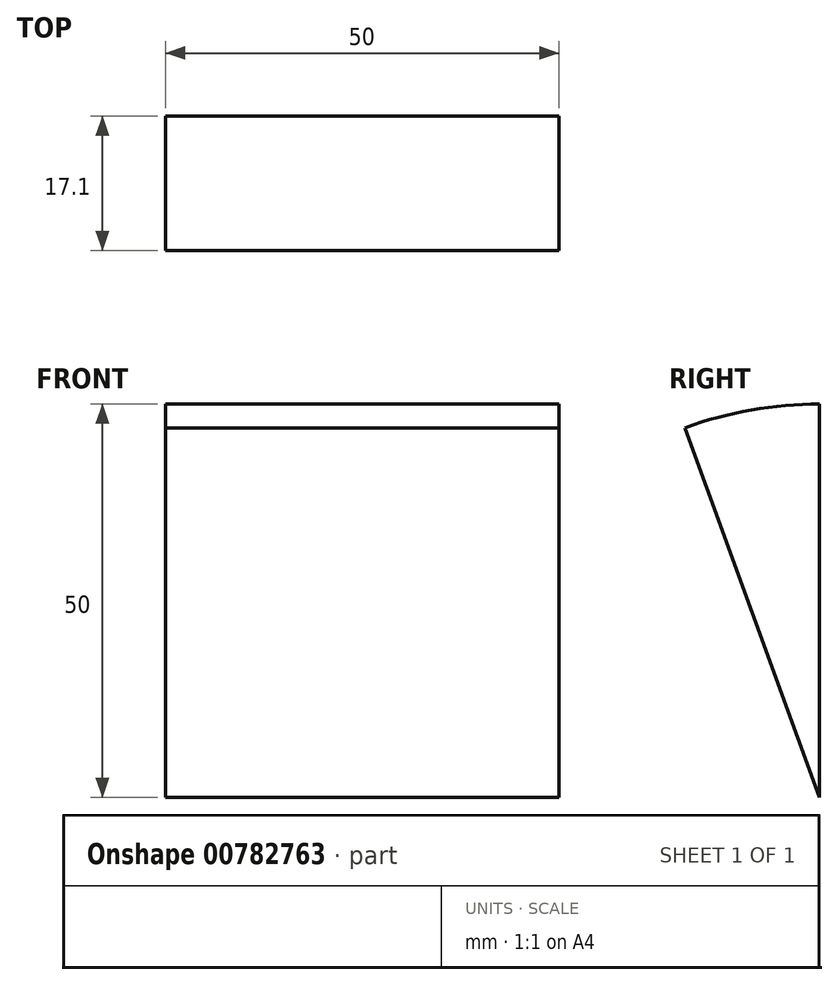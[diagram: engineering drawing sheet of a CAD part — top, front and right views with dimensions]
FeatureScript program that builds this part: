
annotation { "Feature Type Name" : "Feature", "Feature Type Description" : "" }
export const myFeature = defineFeature(function(context is Context, id is Id, definition is map)
    precondition{}
    {
        {
            var Q0;
            Q0=qCreatedBy(makeId("Front.planeOp"),FACE);
            var sketch = newSketch(context, id + "F0", { "sketchPlane" : qUnion([Q0])});
            skLineSegment(sketch, "E0.bottom", {"start": v(0, 0) * mm, "end": v(50, 0) * mm});
            skLineSegment(sketch, "E0.top", {"start": v(0, 50) * mm, "end": v(50, 50) * mm});
            skLineSegment(sketch, "E0.left", {"start": v(0, 0) * mm, "end": v(0, 50) * mm});
            skLineSegment(sketch, "E0.right", {"start": v(50, 0) * mm, "end": v(50, 50) * mm});
            skSolve(sketch);
        }
        {
            var Q0;
            Q0=makeQuery(id+"F0.imprint","IMPRINT",FACE,{"disambiguationData":[TD([[makeQuery(id+"F0.imprint","IMPRINT",EDGE,{"derivedFrom":sQuery(id+"F0.wireOp",EDGE,"E0.bottom")}),1.0]])]});
            var Q1;
            Q1=sQuery(id+"F0.wireOp",EDGE,"E0.bottom");
            revolve(context, id + "F1", {"surfaceOperationType" : NewSurfaceOperationType.NEW, "entities" : qUnion([Q0]), "axis" : qUnion([Q1]), "revolveType" : RevolveType.ONE_DIRECTION, "angle" : 20 * degree});
        }
    });
